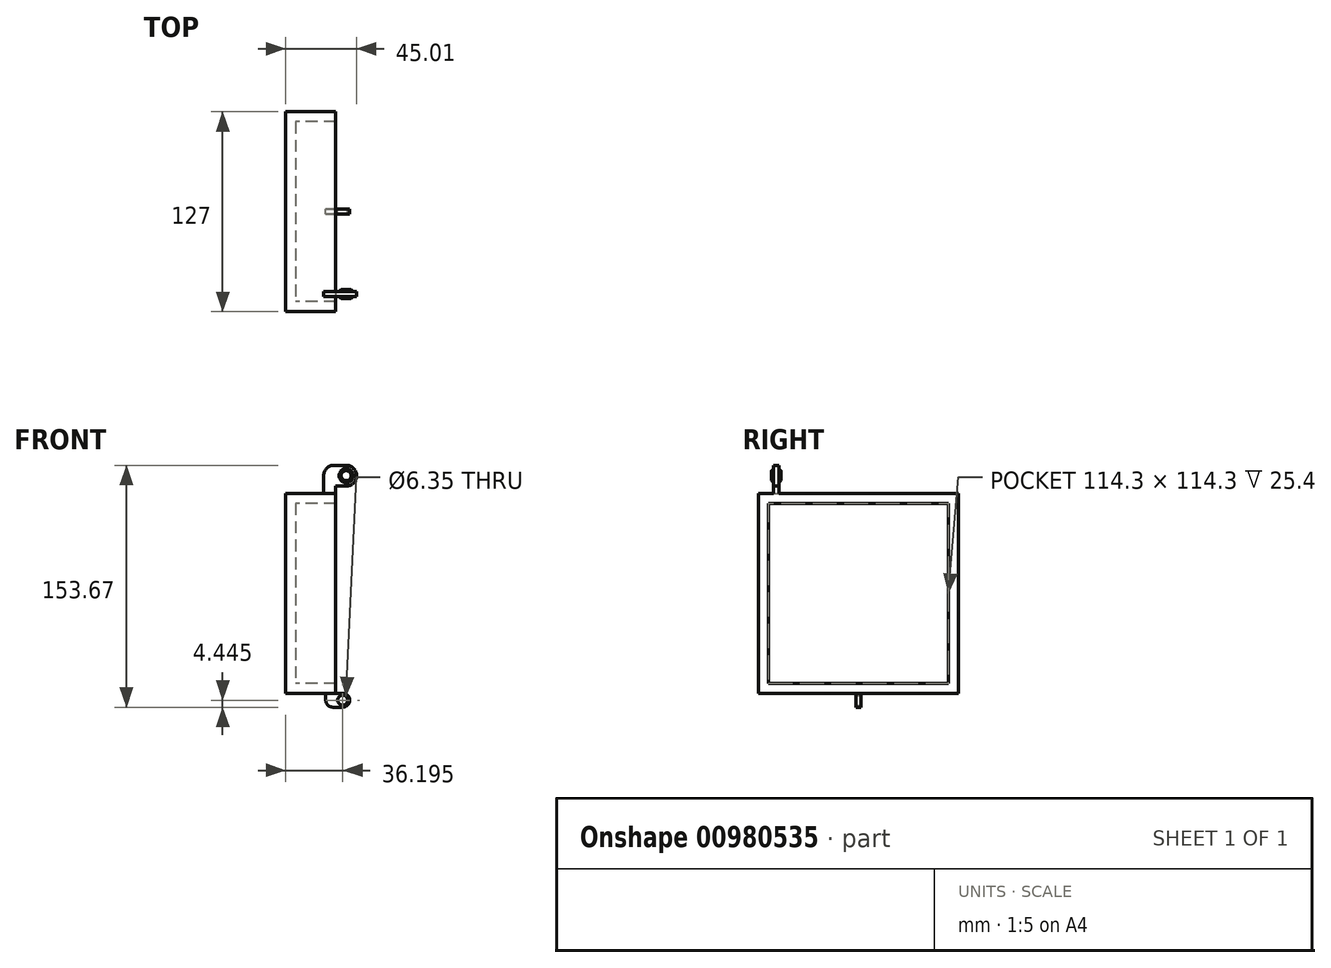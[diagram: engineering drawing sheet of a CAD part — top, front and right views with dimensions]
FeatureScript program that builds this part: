
annotation { "Feature Type Name" : "Feature", "Feature Type Description" : "" }
export const myFeature = defineFeature(function(context is Context, id is Id, definition is map)
    precondition{}
    {
        {
            var Q0;
            Q0=qCreatedBy(makeId("Right.planeOp"),FACE);
            var sketch = newSketch(context, id + "F0", { "sketchPlane" : qUnion([Q0])});
            skLineSegment(sketch, "E0.bottom", {"start": v(63.5, 63.5) * mm, "end": v(-63.5, 63.5) * mm});
            skLineSegment(sketch, "E0.top", {"start": v(63.5, -63.5) * mm, "end": v(-63.5, -63.5) * mm});
            skLineSegment(sketch, "E0.left", {"start": v(63.5, 63.5) * mm, "end": v(63.5, -63.5) * mm});
            skLineSegment(sketch, "E0.right", {"start": v(-63.5, 63.5) * mm, "end": v(-63.5, -63.5) * mm});
            skPoint(sketch, "E0.middle", {"position": v(0, 0) * mm});
            skLineSegment(sketch, "E1.bottom", {"start": v(57.15, 57.15) * mm, "end": v(-57.15, 57.15) * mm});
            skLineSegment(sketch, "E1.top", {"start": v(57.15, -57.15) * mm, "end": v(-57.15, -57.15) * mm});
            skLineSegment(sketch, "E1.left", {"start": v(57.15, 57.15) * mm, "end": v(57.15, -57.15) * mm});
            skLineSegment(sketch, "E1.right", {"start": v(-57.15, 57.15) * mm, "end": v(-57.15, -57.15) * mm});
            skSolve(sketch);
        }
        {
            var Q0;
            Q0=makeQuery(id+"F0.imprint","IMPRINT",FACE,{"disambiguationData":[TD([[makeQuery(id+"F0.imprint","IMPRINT",EDGE,{"derivedFrom":sQuery(id+"F0.wireOp",EDGE,"E0.bottom")}),1.0]])]});
            extrude(context, id + "F1", {"entities" : qUnion([Q0]), "depth" : 25.4 * mm, "offsetDistance" : 25.4 * mm});
        }
        {
            var Q0;
            Q0=qCreatedBy(makeId("Right.planeOp"),FACE);
            var sketch = newSketch(context, id + "F2", { "sketchPlane" : qUnion([Q0])});
            skLineSegment(sketch, "E2.bottom", {"start": v(-63.5, 63.5) * mm, "end": v(63.5, 63.5) * mm});
            skLineSegment(sketch, "E2.top", {"start": v(-63.5, -63.5) * mm, "end": v(63.5, -63.5) * mm});
            skLineSegment(sketch, "E2.left", {"start": v(-63.5, 63.5) * mm, "end": v(-63.5, -63.5) * mm});
            skLineSegment(sketch, "E2.right", {"start": v(63.5, 63.5) * mm, "end": v(63.5, -63.5) * mm});
            skSolve(sketch);
        }
        {
            var Q0;
            Q0 = qSketchRegion(id + "F2", true);
            extrude(context, id + "F3", {"entities" : qUnion([Q0]), "operationType" : NewBodyOperationType.ADD, "oppositeDirection" : true, "depth" : 6.35 * mm, "offsetDistance" : 25.4 * mm});
        }
        {
            var Q0;
            Q0=makeQuery(id+"F3.boolean.opBoolean","MERGE",FACE,{"derivedFrom":[makeQuery(id+"F1.opExtrude","SWEPT_FACE",FACE,{"disambiguationData":[OSD([sQuery(id+"F0.wireOp",EDGE,"E0.bottom")])]}),makeQuery(id+"F3.opExtrude","SWEPT_FACE",FACE,{"disambiguationData":[OSD([sQuery(id+"F2.wireOp",EDGE,"E2.bottom")])]})]});
            var sketch = newSketch(context, id + "F4", { "sketchPlane" : qUnion([Q0])});
            skLineSegment(sketch, "E3.bottom", {"start": v(17.78, -53.98) * mm, "end": v(38.66, -53.98) * mm});
            skLineSegment(sketch, "E3.top", {"start": v(17.78, -50.67) * mm, "end": v(38.66, -50.67) * mm});
            skLineSegment(sketch, "E3.left", {"start": v(17.78, -53.98) * mm, "end": v(17.78, -50.67) * mm});
            skLineSegment(sketch, "E3.right", {"start": v(38.66, -53.98) * mm, "end": v(38.66, -50.67) * mm});
            skSolve(sketch);
        }
        {
            var Q0;
            Q0 = qSketchRegion(id + "F4", true);
            extrude(context, id + "F5", {"entities" : qUnion([Q0]), "operationType" : NewBodyOperationType.ADD, "depth" : 17.78 * mm, "offsetDistance" : 25.4 * mm});
        }
        {
            var Q0;
            Q0=makeQuery(id+"F5.opExtrude","CAP_EDGE",EDGE,{"disambiguationData":[OSD([sQuery(id+"F4.wireOp",EDGE,"E3.right")])],"isStart":false});
            fillet(context, id + "F6", {"entities" : qUnion([Q0]), "radius" : 6.63 * mm, "tangentPropagation" : true, "allowEdgeOverflow" : false});
        }
        {
            var Q0;
            Q0=makeQuery(id+"F5.opExtrude","SWEPT_FACE",FACE,{"disambiguationData":[OSD([sQuery(id+"F4.wireOp",EDGE,"E3.bottom")])]});
            var sketch = newSketch(context, id + "F7", { "sketchPlane" : qUnion([Q0])});
            skArc(sketch, "E4", {"start": v(32.03, 68.02) * mm, "mid": v(38.66, 74.65) * mm, "end": v(32.03, 81.28) * mm});
            skLineSegment(sketch, "E5", {"start": v(32.03, 68.02) * mm, "end": v(25.4, 68.02) * mm});
            skLineSegment(sketch, "E6", {"start": v(25.4, 68.02) * mm, "end": v(25.4, 63.5) * mm});
            skLineSegment(sketch, "E7", {"start": v(25.4, 63.5) * mm, "end": v(41.4, 57.38) * mm});
            skLineSegment(sketch, "E8", {"start": v(41.4, 57.38) * mm, "end": v(43.72, 87.8) * mm});
            skLineSegment(sketch, "E9", {"start": v(43.72, 87.8) * mm, "end": v(32.03, 81.28) * mm});
            skSolve(sketch);
        }
        {
            var Q0;
            Q0 = qSketchRegion(id + "F7", true);
            extrude(context, id + "F8", {"entities" : qUnion([Q0]), "operationType" : NewBodyOperationType.REMOVE, "oppositeDirection" : true, "depth" : 6.35 * mm, "offsetDistance" : 25.4 * mm});
        }
        {
            var Q0;
            Q0=makeQuery(id+"F5.opExtrude","CAP_EDGE",EDGE,{"disambiguationData":[OSD([sQuery(id+"F4.wireOp",EDGE,"E3.left")])],"isStart":false});
            fillet(context, id + "F9", {"entities" : qUnion([Q0]), "radius" : 6.63 * mm, "tangentPropagation" : true, "allowEdgeOverflow" : false});
        }
        {
            var Q0;
            Q0=makeQuery(id+"F5.opExtrude","SWEPT_FACE",FACE,{"disambiguationData":[OSD([sQuery(id+"F4.wireOp",EDGE,"E3.bottom")])]});
            var sketch = newSketch(context, id + "F10", { "sketchPlane" : qUnion([Q0])});
            skCircle(sketch, "E10", {"center": v(32.03, 74.65) * mm, "radius": 4.45 * mm});
            skSolve(sketch);
        }
        {
            var Q0;
            Q0 = qSketchRegion(id + "F10", true);
            extrude(context, id + "F11", {"entities" : qUnion([Q0]), "operationType" : NewBodyOperationType.ADD, "depth" : 1.27 * mm, "offsetDistance" : 25.4 * mm});
        }
        {
            var Q0;
            Q0=makeQuery(id+"F5.opExtrude","SWEPT_FACE",FACE,{"disambiguationData":[OSD([sQuery(id+"F4.wireOp",EDGE,"E3.top")])]});
            var sketch = newSketch(context, id + "F12", { "sketchPlane" : qUnion([Q0])});
            skCircle(sketch, "E11", {"center": v(-32.03, 74.65) * mm, "radius": 4.45 * mm});
            skSolve(sketch);
        }
        {
            var Q0;
            Q0 = qSketchRegion(id + "F12", true);
            extrude(context, id + "F13", {"entities" : qUnion([Q0]), "operationType" : NewBodyOperationType.ADD, "depth" : 1.27 * mm, "offsetDistance" : 25.4 * mm});
        }
        {
            var Q0;
            Q0=makeQuery(id+"F11.opExtrude","CAP_EDGE",EDGE,{"disambiguationData":[OSD([sQuery(id+"F10.wireOp",EDGE,"E10")])],"isStart":false});
            var Q1;
            Q1=makeQuery(id+"F13.opExtrude","CAP_EDGE",EDGE,{"disambiguationData":[OSD([sQuery(id+"F12.wireOp",EDGE,"E11")])],"isStart":false});
            chamfer(context, id + "F14", {"entities" : qUnion([Q0, Q1]), "width" : 1.27 * mm, "tangentPropagation" : true});
        }
        {
            var Q0;
            Q0=qCreatedBy(makeId("Front.planeOp"),FACE);
            var sketch = newSketch(context, id + "F15", { "sketchPlane" : qUnion([Q0])});
            skLineSegment(sketch, "E12", {"start": v(19.05, -63.5) * mm, "end": v(19.05, -72.39) * mm});
            skLineSegment(sketch, "E13", {"start": v(19.05, -72.39) * mm, "end": v(34.3, -72.39) * mm});
            skLineSegment(sketch, "E14", {"start": v(34.3, -72.39) * mm, "end": v(34.3, -63.5) * mm});
            skLineSegment(sketch, "E15", {"start": v(34.3, -63.5) * mm, "end": v(19.05, -63.5) * mm});
            skSolve(sketch);
        }
        {
            var Q0;
            Q0 = qSketchRegion(id + "F15", true);
            extrude(context, id + "F16", {"entities" : qUnion([Q0]), "operationType" : NewBodyOperationType.ADD, "endBound" : BoundingType.SYMMETRIC, "depth" : 3.17 * mm, "offsetDistance" : 25.4 * mm});
        }
        {
            var Q0;
            Q0=makeQuery(id+"F16.opExtrude","SWEPT_EDGE",EDGE,{"disambiguationData":[OSD([sQuery(id+"F15.wireOp",EDGE,"E14"),sQuery(id+"F15.wireOp",EDGE,"E15")])]});
            var Q1;
            Q1=makeQuery(id+"F16.opExtrude","SWEPT_EDGE",EDGE,{"disambiguationData":[OSD([sQuery(id+"F15.wireOp",EDGE,"E13"),sQuery(id+"F15.wireOp",EDGE,"E14")])]});
            var Q2;
            Q2=makeQuery(id+"F16.opExtrude","SWEPT_EDGE",EDGE,{"disambiguationData":[OSD([sQuery(id+"F15.wireOp",EDGE,"E12"),sQuery(id+"F15.wireOp",EDGE,"E13")])]});
            fillet(context, id + "F17", {"entities" : qUnion([Q0, Q1, Q2]), "radius" : 4.44 * mm, "tangentPropagation" : true, "allowEdgeOverflow" : false});
        }
        {
            var Q0;
            Q0=makeQuery(id+"F16.opExtrude","CAP_FACE",FACE,{"disambiguationData":[OSD([sQuery(id+"F15.wireOp",EDGE,"E12"),sQuery(id+"F15.wireOp",EDGE,"E13"),sQuery(id+"F15.wireOp",EDGE,"E14"),sQuery(id+"F15.wireOp",EDGE,"E15")])],"isStart":true});
            var sketch = newSketch(context, id + "F18", { "sketchPlane" : qUnion([Q0])});
            skCircle(sketch, "E16", {"center": v(-29.85, -67.94) * mm, "radius": 3.18 * mm});
            skSolve(sketch);
        }
        {
            var Q0;
            Q0 = qSketchRegion(id + "F18", true);
            extrude(context, id + "F19", {"entities" : qUnion([Q0]), "operationType" : NewBodyOperationType.REMOVE, "oppositeDirection" : true, "depth" : 25.4 * mm, "offsetDistance" : 25.4 * mm});
        }
    });
